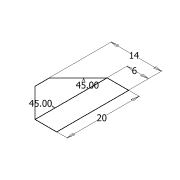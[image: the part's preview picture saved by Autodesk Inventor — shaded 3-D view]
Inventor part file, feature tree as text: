
AUTODESK INVENTOR PART (.ipt)
format: ipt  version: 2022 (Build 260153000, 153)  size: 71,680 bytes
history: native  units: mm
features: sketch x1
ambient origin geometry x8: Origin, YZ Plane, XZ Plane, XY Plane, X Axis, Y Axis, Z Axis, Center Point
feature tree (1):
  sketch  "Sketch1"  dims[d0=20.0mm d1=45.0deg d2=45.0deg d4=14.0mm d5=6.0mm]
